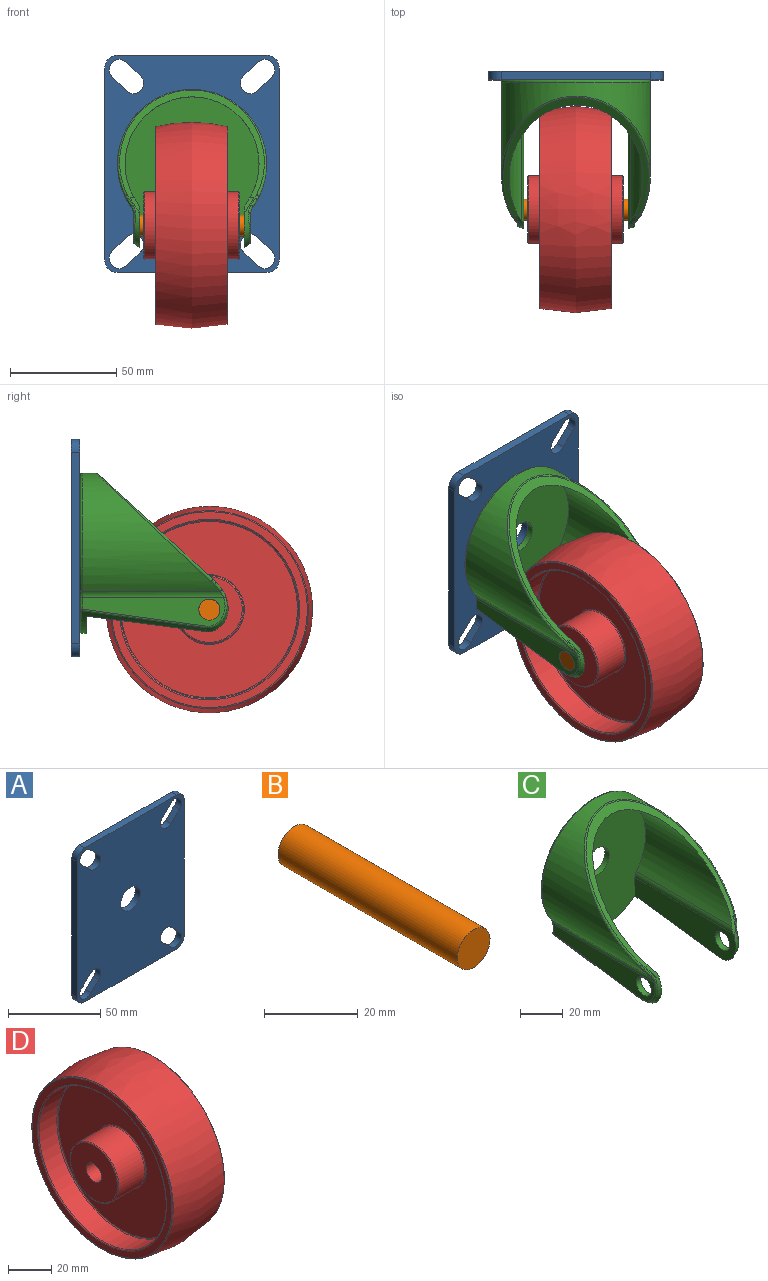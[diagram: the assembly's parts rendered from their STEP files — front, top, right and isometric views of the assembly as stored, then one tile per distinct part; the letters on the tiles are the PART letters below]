
ASSEMBLY  parts=4 mates=3
PART A: 27 faces, bbox 82x4x102 mm
  f0: cylinder r=4.75mm len=8.62mm, axis (0,1,0), area 64.7mm2, adj f1,f20,f21,f22
  f1: plane 6.02x5.77mm, normal (0.69,0,0.72), area 33.4mm2, adj f0,f2,f21,f22
  f2: cylinder r=4.75mm len=8.29mm, axis (0,1,0), area 60.7mm2, adj f1,f20,f21,f22
  f3: cylinder r=4.75mm len=8.62mm, axis (0,1,0), area 64.7mm2, adj f4,f15,f21,f22
  f4: plane 6.4x6.27mm, normal (0.7,0,-0.71), area 35.8mm2, adj f3,f5,f21,f22
  f5: cylinder r=4.75mm len=8.29mm, axis (0,1,0), area 60.7mm2, adj f4,f15,f21,f22
  f6: plane 6.02x5.77mm, normal (0.69,0,-0.72), area 33.4mm2, adj f7,f16,f21,f22
  f7: cylinder r=4.75mm len=8.62mm, axis (0,1,0), area 64.7mm2, adj f6,f8,f21,f22
  f8: plane 6.4x6.27mm, normal (-0.7,0,0.71), area 35.8mm2, adj f7,f16,f21,f22
  f9: plane 90x4mm, normal (1,0,0), area 360mm2, adj f21,f22,f24,f26
  f10: plane 70x4mm, normal (0,0,1), area 280mm2, adj f21,f22,f23,f24
  f11: plane 90x4mm, normal (-1,0,0), area 360mm2, adj f21,f22,f23,f25
  f12: cylinder r=4.75mm len=8.62mm, axis (0,1,0), area 64.7mm2, adj f13,f18,f21,f22
  f13: plane 6.02x5.77mm, normal (-0.69,0,-0.72), area 33.4mm2, adj f12,f14,f21,f22
  f14: cylinder r=4.75mm len=8.29mm, axis (0,1,0), area 60.7mm2, adj f13,f18,f21,f22
  f15: plane 6.02x5.77mm, normal (-0.69,0,0.72), area 33.4mm2, adj f3,f5,f21,f22
  f16: cylinder r=4.75mm len=8.29mm, axis (0,1,0), area 60.7mm2, adj f6,f8,f21,f22
  f17: plane 70x4mm, normal (0,0,-1), area 280mm2, adj f21,f22,f25,f26
  f18: plane 6.4x6.27mm, normal (0.7,0,0.71), area 35.8mm2, adj f12,f14,f21,f22
  f19: cylinder r=7.5mm len=15mm, axis (0,1,0), area 188.5mm2, adj f21,f22
  f20: plane 6.4x6.27mm, normal (-0.7,0,-0.71), area 35.8mm2, adj f0,f2,f21,f22
  f21: plane 102x82mm, normal (0,-1,0), area 7517.4mm2, adj f0,f1,f2,f3,f4,f5,f6,f7
  f22: plane 102x82mm, normal (0,1,0), area 7517.4mm2, adj f0,f1,f2,f3,f4,f5,f6,f7
  f23: cylinder r=6mm len=6mm, axis (0,-1,0), area 37.7mm2, adj f10,f11,f21,f22
  f24: cylinder r=6mm len=6mm, axis (0,1,0), area 37.7mm2, adj f9,f10,f21,f22
  f25: cylinder r=6mm len=6mm, axis (0,1,0), area 37.7mm2, adj f11,f17,f21,f22
  f26: cylinder r=6mm len=6mm, axis (0,-1,0), area 37.7mm2, adj f9,f17,f21,f22
PART B: 3 faces, bbox 9.9x54x9.9 mm
  f0: cylinder r=4.95mm len=54mm, axis (0,1,0), area 1679.5mm2, adj f1,f2
  f1: plane 9.9x9.9mm, normal (0,-1,0), area 77mm2, adj f0
  f2: plane 9.9x9.9mm, normal (0,1,0), area 77mm2, adj f0
PART C: 42 faces, bbox 119.1x88.5x85.4 mm
  f0: cylinder r=31.5mm len=63.07mm, axis (0,1,0), area 4249.3mm2, adj f1,f2,f10,f11,f14,f15
  f1: cylinder r=20mm len=7.72mm, axis (-1,0,0), area 12.7mm2, adj f0,f6,f10,f14,f19
  f2: cylinder r=20mm len=7.72mm, axis (-1,0,0), area 12.7mm2, adj f0,f7,f10,f15,f16
  f3: cylinder r=35mm len=70mm, axis (0,1,0), area 4611.7mm2, adj f12,f13,f22,f34,f35,f36,f37,f38
  f4: plane 73.11x68mm, normal (0,1,0), area 3758.5mm2, adj f20,f21,f22,f23,f24,f25,f39
  f5: plane 67.15x13.45mm, normal (1,0,0), area 573.8mm2, adj f13,f24,f28,f30,f41
  f6: plane 66.62x17.84mm, normal (-1,0,0), area 877.4mm2, adj f1,f9,f11,f14,f19,f41
  f7: plane 66.62x17.83mm, normal (1,0,0), area 877.4mm2, adj f2,f9,f11,f15,f16,f40
  f8: plane 67.15x13.45mm, normal (-1,0,0), area 573.8mm2, adj f12,f20,f29,f31,f40
  f9: bspline ~70x55mm, area 497mm2, adj f6,f7,f11,f16,f19,f25,f28,f29
  f10: plane 68x55.17mm, normal (0,-0.67,0.74), area 566.9mm2, adj f0,f1,f2,f17,f18,f38
  f11: plane 71.89x63.06mm, normal (0,-1,0), area 3417.9mm2, adj f0,f6,f7,f9,f14,f15,f39
  f12: cylinder r=5mm len=66.51mm, axis (0,1,0), area 204.2mm2, adj f3,f8,f21,f33
  f13: cylinder r=5mm len=66.51mm, axis (0,1,0), area 204.2mm2, adj f3,f5,f23,f32
  f14: cylinder r=5mm len=64.88mm, axis (0,1,0), area 201.4mm2, adj f0,f1,f6,f11
  f15: cylinder r=5mm len=64.88mm, axis (0,1,0), area 201.4mm2, adj f0,f2,f7,f11
  f16: bspline ~30.96x26.73mm, area 65.6mm2, adj f2,f7,f9,f17,f31,f33,f35
  f17: bspline ~33.43x33.4mm, area 0.8mm2, adj f10,f16,f37
  f18: bspline ~33.43x33.4mm, area 0.8mm2, adj f10,f19,f36
  f19: bspline ~31.4x26.64mm, area 63.3mm2, adj f1,f6,f9,f18,f30,f32,f34
  f20: cylinder r=1mm len=5.43mm, axis (0,0,1), area 8.5mm2, adj f4,f8,f21,f27
  f21: torus R=6mm, axis (0,-1,0), area 5.2mm2, adj f4,f12,f20,f22
  f22: torus R=34mm, axis (0,-1,0), area 238.6mm2, adj f3,f4,f21,f23
  f23: torus R=6mm, axis (0,-1,0), area 5.2mm2, adj f4,f13,f22,f24
  f24: cylinder r=1mm len=5.43mm, axis (0,0,1), area 8.5mm2, adj f4,f5,f23,f26
  f25: bspline ~55.55x11.92mm, area 86.7mm2, adj f4,f9,f26,f27
  f26: sphere r=1mm, area 1mm2, adj f24,f25,f28
  f27: sphere r=1mm, area 0.8mm2, adj f20,f25,f29
  f28: bspline ~83.86x12.3mm, area 51.9mm2, adj f5,f9,f26,f30
  f29: bspline ~83.86x12.3mm, area 51.9mm2, adj f8,f9,f27,f31
  f30: bspline ~16.11x12.35mm, area 22.5mm2, adj f5,f19,f28,f32
  f31: bspline ~16.11x12.35mm, area 22.5mm2, adj f8,f16,f29,f33
  f32: bspline ~6.06x3.86mm, area 6.5mm2, adj f13,f19,f30,f34
  f33: bspline ~6.06x3.86mm, area 6.5mm2, adj f12,f16,f31,f35
  f34: bspline ~5.8x5.15mm, area 8.9mm2, adj f3,f19,f32,f36
  f35: bspline ~5.8x5.15mm, area 8.9mm2, adj f3,f16,f33,f37
  f36: bspline ~8.97x8.7mm, area 4.4mm2, adj f3,f18,f34,f38
  f37: bspline ~6.72x6.43mm, area 4.4mm2, adj f3,f17,f35,f38
  f38: bspline ~69.96x54.53mm, area 229.1mm2, adj f3,f10,f36,f37
  f39: cylinder r=7.5mm len=15mm, axis (0,1,0), area 141.4mm2, adj f4,f11
  f40: cylinder r=4.95mm len=9.9mm, axis (1,0,0), area 93.3mm2, adj f7,f8
  f41: cylinder r=4.95mm len=9.9mm, axis (1,0,0), area 93.3mm2, adj f5,f6
PART D: 22 faces, bbox 44.8x100.7x100.7 mm
  f0: cylinder r=41.9mm len=83.81mm, axis (-1,0,0), area 3078.2mm2, adj f12,f19
  f1: plane 82.81x82.81mm, normal (-1,0,0), area 4540.2mm2, adj f12,f13
  f2: cylinder r=15.9mm len=31.81mm, axis (-1,0,0), area 1698.7mm2, adj f13,f20
  f3: plane 30.81x30.81mm, normal (-1,0,0), area 666.9mm2, adj f4,f20
  f4: cylinder r=5mm len=44.8mm, axis (-1,0,0), area 1407.4mm2, adj f3,f5
  f5: plane 30.81x30.81mm, normal (1,0,0), area 666.9mm2, adj f4,f21
  f6: cylinder r=15.9mm len=31.81mm, axis (-1,0,0), area 1698.7mm2, adj f14,f21
  f7: plane 82.81x82.81mm, normal (1,0,0), area 4540.2mm2, adj f14,f15
  f8: cylinder r=41.9mm len=83.81mm, axis (-1,0,0), area 3078.2mm2, adj f15,f16
  f9: plane 92.02x92.02mm, normal (1,0,0), area 1001.9mm2, adj f16,f17
  f10: revolved ~96.96x96.96mm, area 10133.4mm2, adj f17,f18
  f11: plane 92.02x92.02mm, normal (-1,0,0), area 1001.9mm2, adj f18,f19
  f12: torus R=41.4mm, axis (-1,0,0), area 205.9mm2, adj f0,f1
  f13: torus R=16.4mm, axis (-1,0,0), area 79.4mm2, adj f1,f2
  f14: torus R=16.4mm, axis (-1,0,0), area 79.4mm2, adj f6,f7
  f15: torus R=41.4mm, axis (-1,0,0), area 205.9mm2, adj f7,f8
  f16: torus R=42.4mm, axis (-1,0,0), area 207.7mm2, adj f8,f9
  f17: torus R=46.01mm, axis (-1,0,0), area 194.1mm2, adj f9,f10
  f18: torus R=46.01mm, axis (-1,0,0), area 194.1mm2, adj f10,f11
  f19: torus R=42.4mm, axis (-1,0,0), area 207.7mm2, adj f0,f11
  f20: torus R=15.4mm, axis (-1,0,0), area 77.6mm2, adj f2,f3
  f21: torus R=15.4mm, axis (-1,0,0), area 77.6mm2, adj f5,f6
PLACE A t=(-9.03,-22.84,-43.94)mm
PLACE B rot(axis=(0,0,-1),90deg) t=(9.1,-87.64,-31.77)mm
PLACE C t=(-17.67,-26.84,-2.83)mm
PLACE D t=(-17.9,-87.64,-31.77)mm
MATE slider B.f0 <-> C.f40  axis (1,0,0) through (-44.9,-87.64,-31.77)mm
MATE revolute B.f0 <-> D.f0  axis (1,0,0) through (-17.9,-87.64,-31.77)mm
MATE revolute A.f19 <-> C.f3  axis (0,-1,0) through (-17.67,-26.84,-2.83)mm
